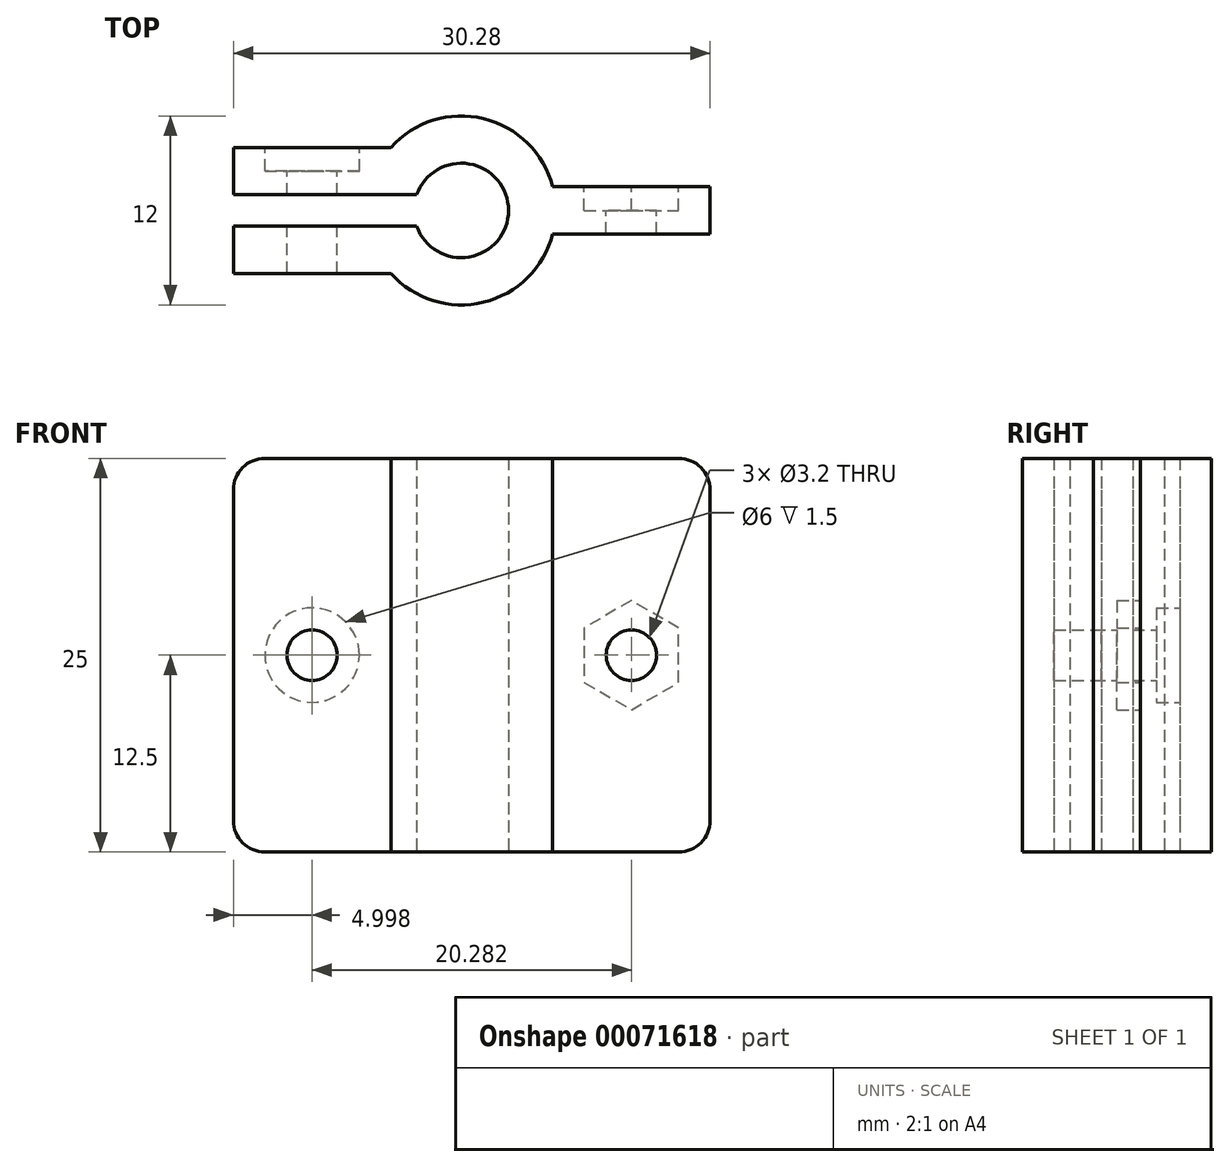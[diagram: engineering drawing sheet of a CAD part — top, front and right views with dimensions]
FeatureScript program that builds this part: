
annotation { "Feature Type Name" : "Feature", "Feature Type Description" : "" }
export const myFeature = defineFeature(function(context is Context, id is Id, definition is map)
    precondition{}
    {
        {
            var Q0;
            Q0=qCreatedBy(makeId("Top.planeOp"),FACE);
            var sketch = newSketch(context, id + "F0", { "sketchPlane" : qUnion([Q0])});
            skArc(sketch, "E0", {"start": v(-2.83, -1) * mm, "mid": v(3, 0) * mm, "end": v(-2.83, 1) * mm});
            skArc(sketch, "E1", {"start": v(-4.47, -4) * mm, "mid": v(1.42, -5.83) * mm, "end": v(5.8, -1.5) * mm});
            skLineSegment(sketch, "E2.bottom", {"start": v(-2.83, 1) * mm, "end": v(-14.47, 1) * mm});
            skLineSegment(sketch, "E2.right", {"start": v(-14.47, 1) * mm, "end": v(-14.47, 4) * mm});
            skLineSegment(sketch, "E3", {"start": v(0, 0) * mm, "end": v(-15.35, 0) * mm, "construction": true});
            skLineSegment(sketch, "E4.MirrorCS", {"start": v(-2.83, -1) * mm, "end": v(-14.47, -1) * mm});
            skLineSegment(sketch, "E5.MirrorCS", {"start": v(-14.47, -1) * mm, "end": v(-14.47, -4) * mm});
            skLineSegment(sketch, "E6.trimOffspring", {"start": v(-4.47, 4) * mm, "end": v(-14.47, 4) * mm});
            skLineSegment(sketch, "E7.MirrorCS", {"start": v(-4.47, -4) * mm, "end": v(-14.47, -4) * mm});
            skLineSegment(sketch, "E8.bottom", {"start": v(5.8, 1.5) * mm, "end": v(15.8, 1.5) * mm});
            skLineSegment(sketch, "E8.top", {"start": v(5.8, -1.5) * mm, "end": v(15.8, -1.5) * mm});
            skLineSegment(sketch, "E8.right", {"start": v(15.8, 1.5) * mm, "end": v(15.8, -1.5) * mm});
            skPoint(sketch, "E9.orphan", {"position": v(0, 1.5) * mm});
            skArc(sketch, "E10.trimOffspring", {"start": v(5.8, 1.5) * mm, "mid": v(1.42, 5.83) * mm, "end": v(-4.47, 4) * mm});
            skSolve(sketch);
        }
        {
            var Q0;
            Q0=makeQuery(id+"F0.imprint","IMPRINT",FACE,{"disambiguationData":[TD([[makeQuery(id+"F0.imprint","IMPRINT",EDGE,{"derivedFrom":sQuery(id+"F0.wireOp",EDGE,"E0")}),-1.0]])]});
            extrude(context, id + "F1", {"entities" : qUnion([Q0]), "depth" : 25 * mm});
        }
        {
            var Q0;
            Q0=makeQuery(id+"F1.opExtrude","SWEPT_FACE",FACE,{"disambiguationData":[OSD([sQuery(id+"F0.wireOp",EDGE,"E6.trimOffspring")])]});
            var sketch = newSketch(context, id + "F2", { "sketchPlane" : qUnion([Q0])});
            skCircle(sketch, "E11", {"center": v(9.47, 12.5) * mm, "radius": 1.6 * mm});
            skPoint(sketch, "E11.centerSnap0", {"position": v(14.47, 12.5) * mm});
            skCircle(sketch, "E12", {"center": v(9.47, 12.5) * mm, "radius": 3 * mm});
            skLineSegment(sketch, "E13", {"start": v(9.47, 12.5) * mm, "end": v(9.47, 25) * mm, "construction": true});
            skSolve(sketch);
        }
        {
            var Q0;
            Q0=makeQuery(id+"F2.imprint","IMPRINT",FACE,{"disambiguationData":[TD([[makeQuery(id+"F2.imprint","IMPRINT",EDGE,{"derivedFrom":sQuery(id+"F2.wireOp",EDGE,"E11")}),1.0]])]});
            extrude(context, id + "F3", {"entities" : qUnion([Q0]), "operationType" : NewBodyOperationType.REMOVE, "endBound" : BoundingType.THROUGH_ALL, "oppositeDirection" : true, "depth" : 25 * mm});
        }
        {
            var Q0;
            Q0=makeQuery(id+"F2.imprint","IMPRINT",FACE,{"disambiguationData":[TD([[makeQuery(id+"F2.imprint","IMPRINT",EDGE,{"derivedFrom":sQuery(id+"F2.wireOp",EDGE,"E11")}),-1.0]])]});
            extrude(context, id + "F4", {"entities" : qUnion([Q0]), "operationType" : NewBodyOperationType.REMOVE, "oppositeDirection" : true, "depth" : 1.5 * mm});
        }
        {
            var Q0;
            Q0=makeQuery(id+"F1.opExtrude","CAP_EDGE",EDGE,{"disambiguationData":[OSD([sQuery(id+"F0.wireOp",EDGE,"E2.right")])],"isStart":true});
            var Q1;
            Q1=makeQuery(id+"F1.opExtrude","CAP_EDGE",EDGE,{"disambiguationData":[OSD([sQuery(id+"F0.wireOp",EDGE,"E5.MirrorCS")])],"isStart":true});
            var Q2;
            Q2=makeQuery(id+"F1.opExtrude","CAP_EDGE",EDGE,{"disambiguationData":[OSD([sQuery(id+"F0.wireOp",EDGE,"E5.MirrorCS")])],"isStart":false});
            var Q3;
            Q3=makeQuery(id+"F1.opExtrude","CAP_EDGE",EDGE,{"disambiguationData":[OSD([sQuery(id+"F0.wireOp",EDGE,"E2.right")])],"isStart":false});
            fillet(context, id + "F5", {"entities" : qUnion([Q0, Q1, Q2, Q3]), "radius" : 2 * mm, "tangentPropagation" : true, "allowEdgeOverflow" : false});
        }
        {
            var Q0;
            Q0=makeQuery(id+"F1.opExtrude","SWEPT_FACE",FACE,{"disambiguationData":[OSD([sQuery(id+"F0.wireOp",EDGE,"E8.bottom")])]});
            var sketch = newSketch(context, id + "F6", { "sketchPlane" : qUnion([Q0])});
            skCircle(sketch, "E14", {"center": v(-10.8, 12.5) * mm, "radius": 1.6 * mm});
            skPoint(sketch, "E14.centerSnap0", {"position": v(-15.8, 12.5) * mm});
            skPoint(sketch, "E15", {"position": v(-10.8, 0) * mm});
            skCircle(sketch, "E16.cCircle", {"center": v(-10.8, 12.5) * mm, "radius": 3 * mm, "construction": true});
            skLineSegment(sketch, "E16.0", {"start": v(-13.8, 10.77) * mm, "end": v(-13.8, 14.23) * mm});
            skLineSegment(sketch, "E16.1", {"start": v(-13.8, 14.23) * mm, "end": v(-10.8, 15.96) * mm});
            skLineSegment(sketch, "E16.2", {"start": v(-10.8, 15.96) * mm, "end": v(-7.8, 14.23) * mm});
            skLineSegment(sketch, "E16.3", {"start": v(-7.8, 14.23) * mm, "end": v(-7.8, 10.77) * mm});
            skLineSegment(sketch, "E16.4", {"start": v(-7.8, 10.77) * mm, "end": v(-10.8, 9.04) * mm});
            skLineSegment(sketch, "E16.5", {"start": v(-10.8, 9.04) * mm, "end": v(-13.8, 10.77) * mm});
            skPoint(sketch, "E16.0.midPoint", {"position": v(-13.8, 12.5) * mm});
            skSolve(sketch);
        }
        {
            var Q0;
            Q0=makeQuery(id+"F6.imprint","IMPRINT",FACE,{"disambiguationData":[TD([[makeQuery(id+"F6.imprint","IMPRINT",EDGE,{"derivedFrom":sQuery(id+"F6.wireOp",EDGE,"E14")}),1.0]])]});
            extrude(context, id + "F7", {"entities" : qUnion([Q0]), "operationType" : NewBodyOperationType.REMOVE, "endBound" : BoundingType.THROUGH_ALL, "oppositeDirection" : true, "depth" : 25 * mm});
        }
        {
            var Q0;
            Q0=makeQuery(id+"F6.imprint","IMPRINT",FACE,{"disambiguationData":[TD([[makeQuery(id+"F6.imprint","IMPRINT",EDGE,{"derivedFrom":sQuery(id+"F6.wireOp",EDGE,"E14")}),-1.0]])]});
            extrude(context, id + "F8", {"entities" : qUnion([Q0]), "operationType" : NewBodyOperationType.REMOVE, "oppositeDirection" : true, "depth" : 1.5 * mm});
        }
        {
            var Q0;
            Q0=makeQuery(id+"F1.opExtrude","CAP_EDGE",EDGE,{"disambiguationData":[OSD([sQuery(id+"F0.wireOp",EDGE,"E8.right")])],"isStart":false});
            var Q1;
            Q1=makeQuery(id+"F1.opExtrude","CAP_EDGE",EDGE,{"disambiguationData":[OSD([sQuery(id+"F0.wireOp",EDGE,"E8.right")])],"isStart":true});
            fillet(context, id + "F9", {"entities" : qUnion([Q0, Q1]), "radius" : 2 * mm, "tangentPropagation" : true, "allowEdgeOverflow" : false});
        }
    });
